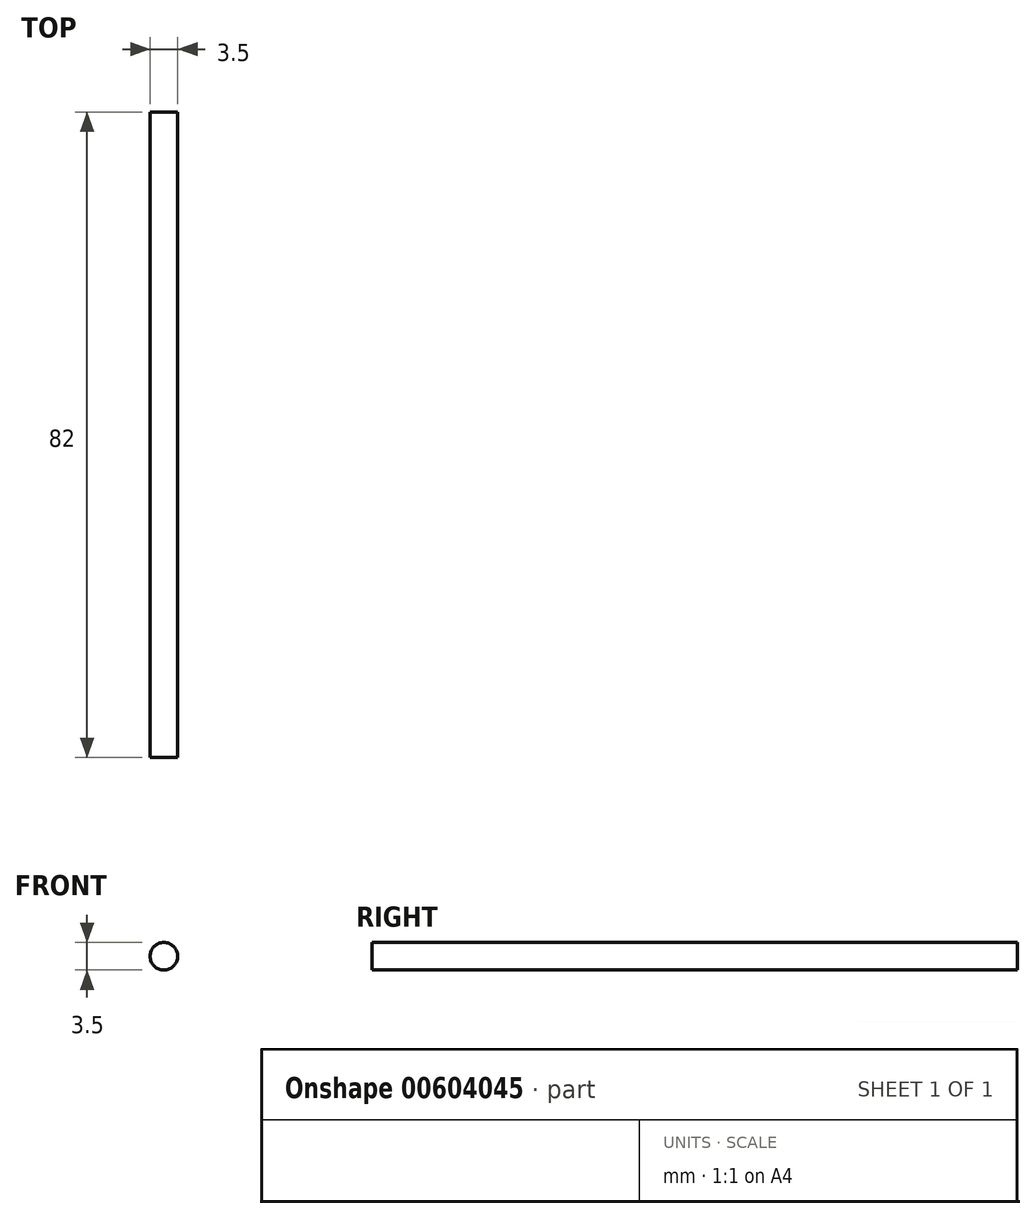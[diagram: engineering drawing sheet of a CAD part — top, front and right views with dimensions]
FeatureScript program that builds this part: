
annotation { "Feature Type Name" : "Feature", "Feature Type Description" : "" }
export const myFeature = defineFeature(function(context is Context, id is Id, definition is map)
    precondition{}
    {
        {
            var Q0;
            Q0=qCreatedBy(makeId("Front.planeOp"),FACE);
            var sketch = newSketch(context, id + "F0", { "sketchPlane" : qUnion([Q0])});
            skCircle(sketch, "E0", {"center": v(0, 0) * mm, "radius": 1.75 * mm});
            skSolve(sketch);
        }
        {
            var Q0;
            Q0=makeQuery(id+"F0.imprint","IMPRINT",FACE,{"disambiguationData":[TD([[makeQuery(id+"F0.imprint","IMPRINT",EDGE,{"derivedFrom":sQuery(id+"F0.wireOp",EDGE,"E0")}),1.0]])]});
            extrude(context, id + "F1", {"entities" : qUnion([Q0]), "depth" : 82 * mm});
        }
    });
